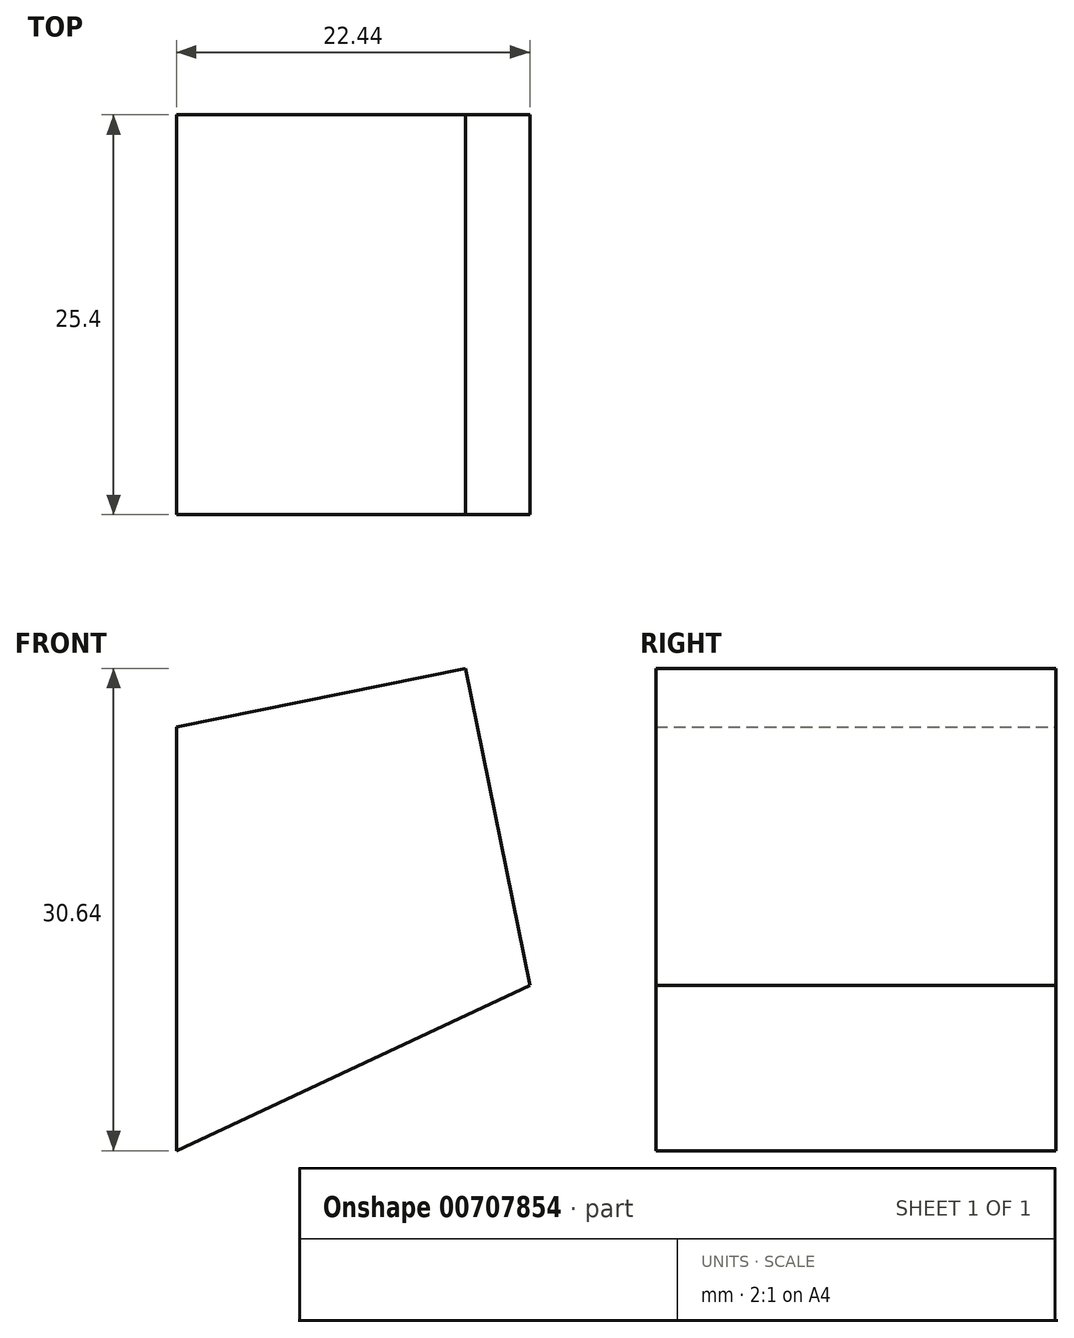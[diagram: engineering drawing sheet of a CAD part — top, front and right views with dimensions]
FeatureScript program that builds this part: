
annotation { "Feature Type Name" : "Feature", "Feature Type Description" : "" }
export const myFeature = defineFeature(function(context is Context, id is Id, definition is map)
    precondition{}
    {
        {
            var Q0;
            Q0=qCreatedBy(makeId("Front.planeOp"),FACE);
            var sketch = newSketch(context, id + "F0", { "sketchPlane" : qUnion([Q0])});
            skLineSegment(sketch, "E0", {"start": v(0, 0) * mm, "end": v(22.44, 10.5) * mm});
            skLineSegment(sketch, "E1", {"start": v(22.44, 10.5) * mm, "end": v(18.34, 30.64) * mm});
            skLineSegment(sketch, "E2", {"start": v(18.34, 30.64) * mm, "end": v(0, 26.9) * mm});
            skLineSegment(sketch, "E3", {"start": v(0, 26.9) * mm, "end": v(0, 0) * mm});
            skSolve(sketch);
        }
        {
            var Q0;
            Q0 = qSketchRegion(id + "F0", true);
            extrude(context, id + "F1", {"entities" : qUnion([Q0]), "endBound" : BoundingType.SYMMETRIC, "depth" : 25.4 * mm, "offsetDistance" : 25.4 * mm});
        }
    });
